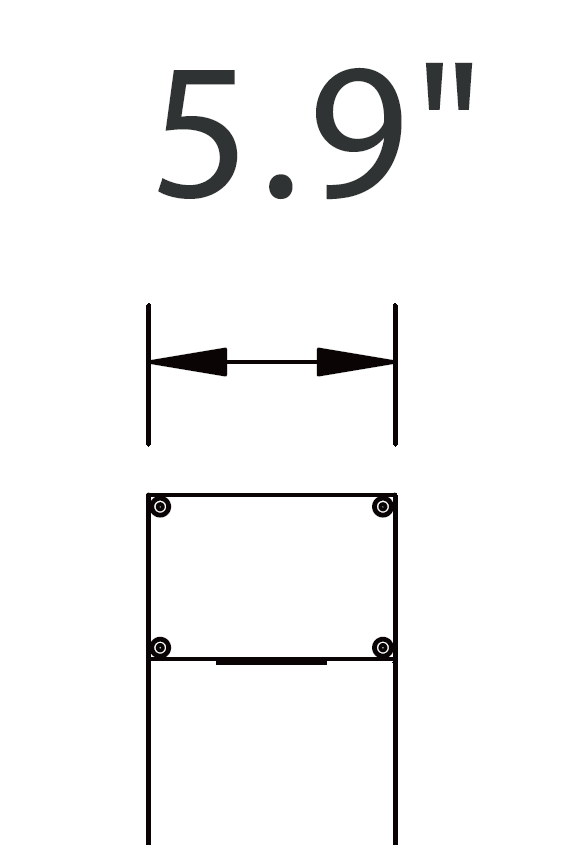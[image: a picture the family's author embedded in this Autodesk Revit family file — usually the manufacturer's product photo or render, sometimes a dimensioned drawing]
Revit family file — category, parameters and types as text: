
# Revit family: Lin1-16.4ft-Double Head
name_source: partatom
category: Lighting Fixtures
units: mm (PartAtom-declared; Revit-internal decimal feet)

## family parameters
Always vertical = Yes
Cut with Voids When Loaded = No
Light Source = No
Maintain Annotation Orientation = No
OmniClass Number = 23.80.70.00
OmniClass Title = Lighting
Part Type = Normal
Room Calculation Point = No
Round Connector Dimension = Use Diameter
Shared = No
Work Plane-Based = No

## types (16) — shared parameters
CRI = 80
Default Elevation = 0' - 0"
H = 16' - 4 13/16"
IP Rating = IP65
Input Voltage = 120-277V
Lamp = LED
Load Classification = Lighting
Manufacturer = Above All Lighting
Power Factor = 0.9
URL = https://www.abovealllighting.com

## per-type parameters (varying)
| type | IES | Model | Wattage Comments |
| LIN1-30W-3000K-II-9.84ft | IES : 30W-II | LIN1-3030801-II-BK | 30W |
| LIN1-30W-3000K-III-9.84ft | IES : 30W-III | LIN1-3030801-III-BK | 30W |
| LIN1-30W-3000K-IV-9.84ft | IES : 30W-IV | LIN1-3030801-IV-BK | 30W |
| LIN1-30W-3000K-V-9.84ft | IES : 30W-V | LIN1-3030801-V-BK | 30W |
| LIN1-40W-3000K-II-9.84ft | IES : 40W-II | LIN1-4030801-II-BK | 40W |
| LIN1-40W-3000K-III-9.84ft | IES : 40W-III | LIN1-4030801-III-BK | 40W |
| LIN1-40W-3000K-IV-9.84ft | IES : 40W-IV | LIN1-4030801-IV-BK | 40W |
| LIN1-40W-3000K-V-9.84ft | IES : 40W-V | LIN1-4030801-V-BK | 40W |
| LIN1-50W-3000K-II-9.84ft | IES : 50W-II | LIN1-5030801-II-BK | 50W |
| LIN1-50W-3000K-III-9.84ft | IES : 50W-III | LIN1-5030801-III-BK | 50W |
| LIN1-50W-3000K-IV-9.84ft | IES : 50W-IV | LIN1-5030801-IV-BK | 50W |
| LIN1-50W-3000K-V-9.84ft | IES : 50W-V | LIN1-5030801-V-BK | 50W |
| LIN1-60W-3000K-II-9.84ft | IES : 60W-II | LIN1-6030801-II-BK | 60W |
| LIN1-60W-3000K-III-9.84ft | IES : 60W-III | LIN1-6030801-III-BK | 60W |
| LIN1-60W-3000K-IV-9.84ft | IES : 60W-IV | LIN1-6030801-IV-BK | 60W |
| LIN1-60W-3000K-V-9.84ft | IES : 60W-V | LIN1-6030801-V-BK | 60W |

## geometry (parser evidence)
native form markers: Sweep x4
no freeform markers — native parametric forms only
